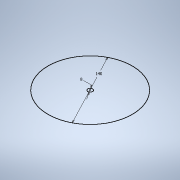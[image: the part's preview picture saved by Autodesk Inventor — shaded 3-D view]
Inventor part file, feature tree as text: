
AUTODESK INVENTOR PART (.ipt)
format: ipt  version: 2022.3 (Build 263350000, 350)  size: 151,552 bytes
history: native  units: mm
features: sketch x3, extrude x2, fillet x2, emboss x1
ambient origin geometry x8: Origin, YZ Plane, XZ Plane, XY Plane, X Axis, Y Axis, Z Axis, Center Point
bodies: Body1 (feature_tree)
feature tree (8):
  extrude  "Extrusion3"  Depth=2.0mm TaperAngle=0.0deg
  extrude  "Extrusion4"  Depth=14.0mm TaperAngle=0.0deg
  fillet  "Fillet2"  Radius=6.0mm
  fillet  "Fillet3"  Radius=2.0mm
  emboss  "Emboss2"
  sketch  "Sketch1"  dims[d0=65.0mm d15=2.0mm d16=0.0mm]
  sketch  "Sketch3"  dims[d17=8.0mm d18=14.0mm d19=0.0mm d20=6.0mm d21=2.0mm]
  sketch  "Sketch4"  dims[d22=65.0mm d23=65.0mm d24=65.0mm d25=65.0mm d26=0.0mm d27=0.0mm d28=1.0mm d29=0.0mm d6=0.0mm d7=0.0mm d8=0.0mm d9=0.0mm]
